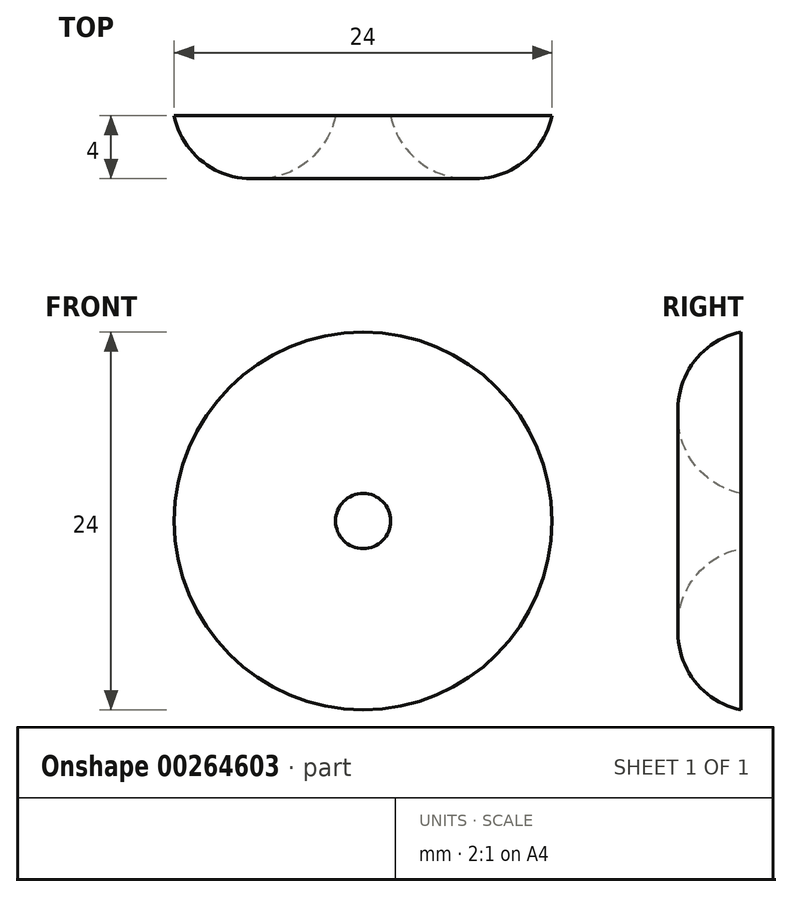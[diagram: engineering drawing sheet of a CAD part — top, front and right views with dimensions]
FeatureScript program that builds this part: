
annotation { "Feature Type Name" : "Feature", "Feature Type Description" : "" }
export const myFeature = defineFeature(function(context is Context, id is Id, definition is map)
    precondition{}
    {
        {
            var Q0;
            Q0=qCreatedBy(makeId("Front.planeOp"),FACE);
            var sketch = newSketch(context, id + "F0", { "sketchPlane" : qUnion([Q0])});
            skCircle(sketch, "E0", {"center": v(0, 0) * mm, "radius": 12 * mm});
            skCircle(sketch, "E1", {"center": v(0, 0) * mm, "radius": 1.75 * mm});
            skSolve(sketch);
        }
        {
            var Q0;
            Q0=makeQuery(id+"F0.imprint","IMPRINT",FACE,{"disambiguationData":[TD([[makeQuery(id+"F0.imprint","IMPRINT",EDGE,{"derivedFrom":sQuery(id+"F0.wireOp",EDGE,"E0")}),1.0]])]});
            extrude(context, id + "F1", {"entities" : qUnion([Q0]), "depth" : 4 * mm});
        }
        {
            var Q0;
            Q0=makeQuery(id+"F1.opExtrude","CAP_FACE",FACE,{"disambiguationData":[OSD([sQuery(id+"F0.wireOp",EDGE,"E0"),sQuery(id+"F0.wireOp",EDGE,"E1")])],"isStart":false});
            fillet(context, id + "F2", {"entities" : qUnion([Q0]), "radius" : 5 * mm, "tangentPropagation" : true, "allowEdgeOverflow" : false});
        }
    });
